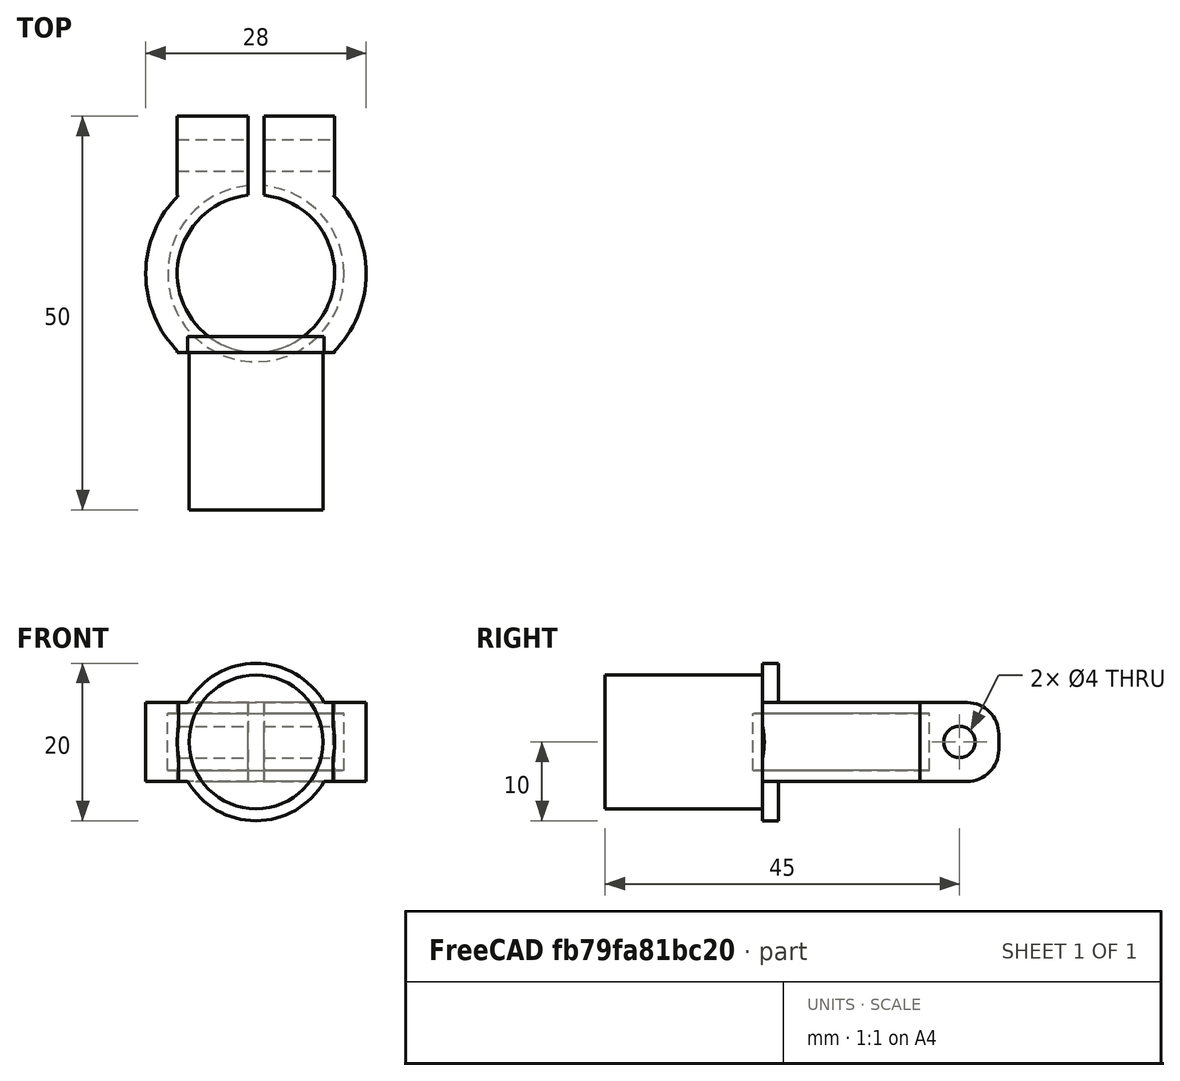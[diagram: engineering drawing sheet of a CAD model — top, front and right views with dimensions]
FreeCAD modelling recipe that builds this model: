
FCSTD DOCUMENT  (FreeCAD 0.18R16110 (Git))
Label: connector-bearing
License: All rights reserved
LicenseURL: http://en.wikipedia.org/wiki/All_rights_reserved
objects: Part::Cylinder×7, Part::Box×3, Part::MultiFuse×2, Part::Cut×2, Part::Fillet×1
note: 15 computed .brp shape members not serialized (recipe doc carries the construction recipe); baked Part::Feature solids carry a one-line shape summary decoded from their .brp

FEATURE [Part::Cylinder] Cylinder004
  Angle = 360
  AttacherType = Attacher::AttachEngine3D
  Height = 20
  Placement = pos=(0,-10,0) rot=(0,0.707107,-0.707107;3.14159rad)
  Radius = 8.5
FEATURE [Part::Cylinder] Cylinder
  Angle = 360
  AttacherType = Attacher::AttachEngine3D
  Height = 7.2
  Placement = pos=(0,0,-3.6) rot=(0,0,1;0rad)
  Radius = 11.2
FEATURE [Part::Cylinder] Cylinder005
  Angle = 360
  AttacherType = Attacher::AttachEngine3D
  Height = 10
  Placement = pos=(0,0,-5) rot=(0,0,1;0rad)
  Radius = 14
FEATURE [Part::Cylinder] Cylinder006
  Angle = 360
  AttacherType = Attacher::AttachEngine3D
  Height = 10
  Placement = pos=(0,0,-5) rot=(0,0,1;0rad)
  Radius = 10
FEATURE [Part::Cylinder] Cylinder007
  Angle = 360
  AttacherType = Attacher::AttachEngine3D
  Height = 2
  Placement = pos=(0,-10,2e-15) rot=(-1,0,0;1.5708rad)
  Radius = 10
FEATURE [Part::Box] Box  label="Cube"
  AttacherType = Attacher::AttachEngine3D
  Height = 10
  Length = 20
  Placement = pos=(-10,10,-5) rot=(0,0,1;0rad)
  Width = 10
FEATURE [Part::MultiFuse] Fusion  label="Positive Fusion"
  Shapes = -> [Cylinder004,Cylinder005,Cylinder007,Box]
FEATURE [Part::Cylinder] Cylinder008
  Angle = 360
  AttacherType = Attacher::AttachEngine3D
  Height = 20
  Placement = pos=(-10,15,-2.2e-15) rot=(0,1,0;1.5708rad)
  Radius = 2
FEATURE [Part::Box] Box001  label="Cube001"
  AttacherType = Attacher::AttachEngine3D
  Height = 10
  Length = 2
  Placement = pos=(-1,5,-5) rot=(0,0,1;0rad)
  Width = 15
FEATURE [Part::Box] Box002  label="Cube002"
  AttacherType = Attacher::AttachEngine3D
  Height = 20
  Length = 20
  Placement = pos=(-10,-20,-10) rot=(0,0,1;0rad)
  Width = 10
FEATURE [Part::Cylinder] Cylinder009
  Angle = 360
  AttacherType = Attacher::AttachEngine3D
  Height = 10
  Placement = pos=(0,-20,4e-15) rot=(-1,0,0;1.5708rad)
  Radius = 8.5
FEATURE [Part::Cut] Cut001
  Base = -> Box002
  Tool = -> Cylinder009
FEATURE [Part::MultiFuse] Fusion001  label="Negative Fusion"
  Shapes = -> [Cylinder006,Cylinder,Cylinder008,Box001,Cut001]
FEATURE [Part::Cut] Cut
  Base = -> Fusion
  Tool = -> Fusion001
FEATURE [Part::Fillet] Fillet
  Base = -> Cut
  Edges = 4 edges r=4: [Edge119,Edge126,Edge131,Edge134]
